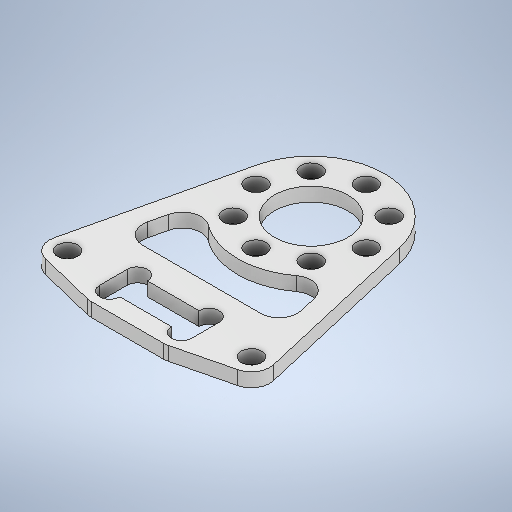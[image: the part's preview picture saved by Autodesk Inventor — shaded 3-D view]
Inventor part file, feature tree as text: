
AUTODESK INVENTOR PART (.ipt)
format: ipt  version: 2025.1 (Build 291241000, 241)  size: 349,696 bytes
history: native  units: mm
features: other x2, extrude x2, sketch x2, fillet x1
ambient origin geometry x8: Origin, YZ Plane, XZ Plane, XY Plane, X Axis, Y Axis, Z Axis, Center Point
bodies: Body1 (feature_tree)
feature tree (7):
  other  "ソリッド1"
  extrude  "押し出し1"  Depth=8.0mm
  extrude  "押し出し2"  Depth=12.0mm
  fillet  "フィレット1"  Radius=16.0mm
  sketch  "スケッチ1"
  other  "スケッチ円形状パターン1"
  sketch  "スケッチ2"
